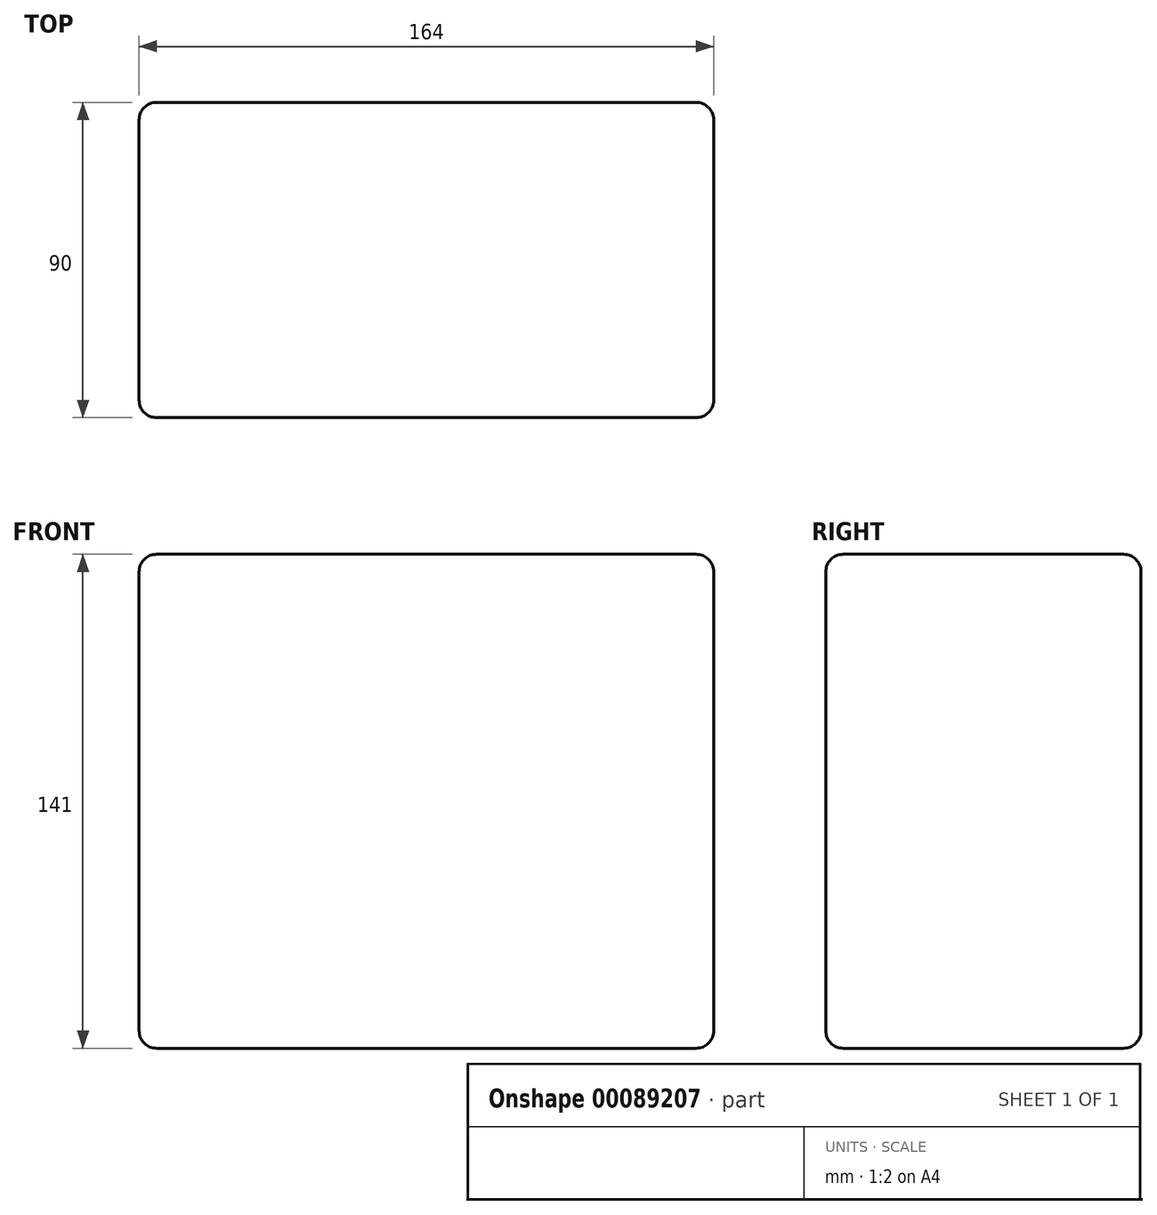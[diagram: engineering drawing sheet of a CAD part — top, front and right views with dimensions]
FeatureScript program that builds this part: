
annotation { "Feature Type Name" : "Feature", "Feature Type Description" : "" }
export const myFeature = defineFeature(function(context is Context, id is Id, definition is map)
    precondition{}
    {
        {
            var Q0;
            Q0=qCreatedBy(makeId("Front.planeOp"),FACE);
            var sketch = newSketch(context, id + "F0", { "sketchPlane" : qUnion([Q0])});
            skLineSegment(sketch, "E0.bottom", {"start": v(0, 0) * mm, "end": v(164, 0) * mm});
            skLineSegment(sketch, "E0.top", {"start": v(0, 141) * mm, "end": v(164, 141) * mm});
            skLineSegment(sketch, "E0.left", {"start": v(0, 0) * mm, "end": v(0, 141) * mm});
            skLineSegment(sketch, "E0.right", {"start": v(164, 0) * mm, "end": v(164, 141) * mm});
            skSolve(sketch);
        }
        {
            var Q0;
            Q0=makeQuery(id+"F0.imprint","IMPRINT",FACE,{"disambiguationData":[TD([[makeQuery(id+"F0.imprint","IMPRINT",EDGE,{"derivedFrom":sQuery(id+"F0.wireOp",EDGE,"E0.bottom")}),1.0]])]});
            extrude(context, id + "F1", {"entities" : qUnion([Q0]), "depth" : 90 * mm});
        }
        {
            var Q0;
            Q0=makeQuery(id+"F1.opExtrude","CAP_FACE",FACE,{"disambiguationData":[OSD([sQuery(id+"F0.wireOp",EDGE,"E0.bottom"),sQuery(id+"F0.wireOp",EDGE,"E0.top"),sQuery(id+"F0.wireOp",EDGE,"E0.left"),sQuery(id+"F0.wireOp",EDGE,"E0.right")])],"isStart":false});
            var Q1;
            Q1=makeQuery(id+"F1.opExtrude","SWEPT_FACE",FACE,{"disambiguationData":[OSD([sQuery(id+"F0.wireOp",EDGE,"E0.top")])]});
            var Q2;
            Q2=makeQuery(id+"F1.opExtrude","SWEPT_FACE",FACE,{"disambiguationData":[OSD([sQuery(id+"F0.wireOp",EDGE,"E0.right")])]});
            var Q3;
            Q3=makeQuery(id+"F1.opExtrude","CAP_FACE",FACE,{"disambiguationData":[OSD([sQuery(id+"F0.wireOp",EDGE,"E0.bottom"),sQuery(id+"F0.wireOp",EDGE,"E0.top"),sQuery(id+"F0.wireOp",EDGE,"E0.left"),sQuery(id+"F0.wireOp",EDGE,"E0.right")])],"isStart":true});
            var Q4;
            Q4=makeQuery(id+"F1.opExtrude","SWEPT_FACE",FACE,{"disambiguationData":[OSD([sQuery(id+"F0.wireOp",EDGE,"E0.bottom")])]});
            var Q5;
            Q5=makeQuery(id+"F1.opExtrude","SWEPT_FACE",FACE,{"disambiguationData":[OSD([sQuery(id+"F0.wireOp",EDGE,"E0.left")])]});
            fillet(context, id + "F2", {"entities" : qUnion([Q0, Q1, Q2, Q3, Q4, Q5]), "radius" : 5 * mm, "tangentPropagation" : true, "allowEdgeOverflow" : false});
        }
    });
